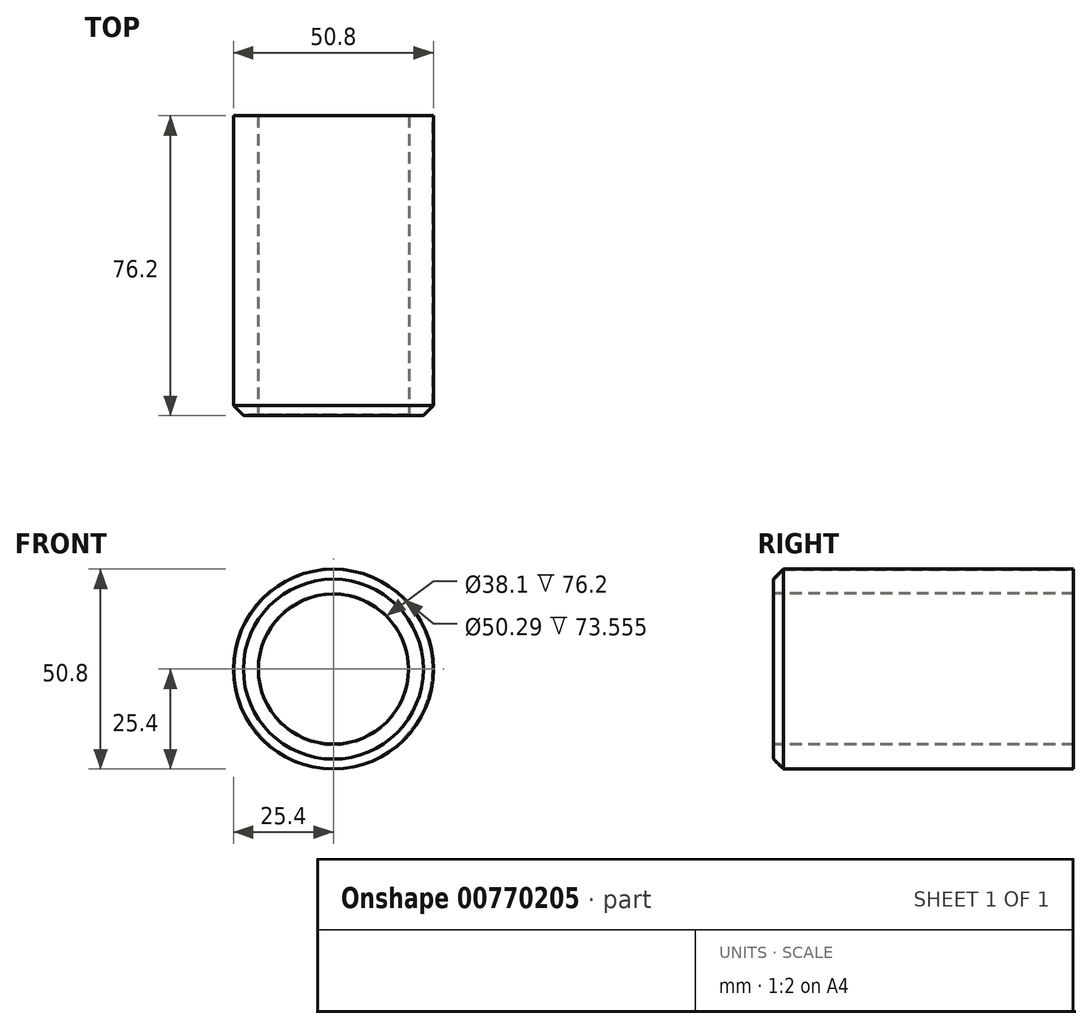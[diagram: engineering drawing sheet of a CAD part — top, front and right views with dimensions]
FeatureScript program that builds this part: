
annotation { "Feature Type Name" : "Feature", "Feature Type Description" : "" }
export const myFeature = defineFeature(function(context is Context, id is Id, definition is map)
    precondition{}
    {
        {
            var Q0;
            Q0=qCreatedBy(makeId("Front.planeOp"),FACE);
            var sketch = newSketch(context, id + "F0", { "sketchPlane" : qUnion([Q0])});
            skCircle(sketch, "E0", {"center": v(0, 0) * mm, "radius": 25.4 * mm});
            skSolve(sketch);
        }
        {
            var Q0;
            Q0 = qSketchRegion(id + "F0", true);
            extrude(context, id + "F1", {"entities" : qUnion([Q0]), "endBound" : BoundingType.SYMMETRIC, "depth" : 76.2 * mm, "offsetDistance" : 25.4 * mm});
        }
        {
            var Q0;
            Q0=makeQuery(id+"F1.opExtrude","CAP_FACE",FACE,{"disambiguationData":[OSD([sQuery(id+"F0.wireOp",EDGE,"E0")])],"isStart":false});
            var sketch = newSketch(context, id + "F2", { "sketchPlane" : qUnion([Q0])});
            skCircle(sketch, "E1", {"center": v(0, 0) * mm, "radius": 19.05 * mm});
            skSolve(sketch);
        }
        {
            var Q0;
            Q0 = qSketchRegion(id + "F2", true);
            extrude(context, id + "F3", {"entities" : qUnion([Q0]), "operationType" : NewBodyOperationType.REMOVE, "endBound" : BoundingType.THROUGH_ALL, "oppositeDirection" : true, "depth" : 25.4 * mm, "offsetDistance" : 25.4 * mm});
        }
        {
            var Q0;
            Q0=makeQuery(id+"F1.opExtrude","CAP_EDGE",EDGE,{"disambiguationData":[OSD([sQuery(id+"F0.wireOp",EDGE,"E0")])],"isStart":false});
            chamfer(context, id + "F4", {"entities" : qUnion([Q0]), "width" : 2.54 * mm, "tangentPropagation" : true});
        }
        {
            var Q0;
            Q0=makeQuery(id+"F1.opExtrude","CAP_FACE",FACE,{"disambiguationData":[OSD([sQuery(id+"F0.wireOp",EDGE,"E0")])],"isStart":true});
            shell(context, id + "F5", {"entities" : qUnion([Q0]), "thickness" : 0.25 * mm});
        }
    });
